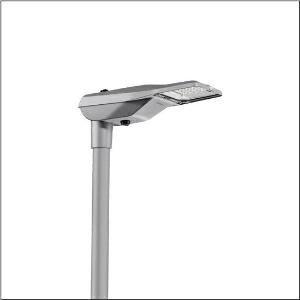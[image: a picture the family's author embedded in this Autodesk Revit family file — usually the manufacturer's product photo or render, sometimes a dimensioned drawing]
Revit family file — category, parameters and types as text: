
# Revit family: streetlight_sl_21_iq_micro___pl52_5xe1h31y08db_0e41
name_source: partatom
category: Lighting Fixtures
units: mm (PartAtom-declared; Revit-internal decimal feet)

## family parameters
Cut with Voids When Loaded = No
Host = Face
Light Source = No
Part Type = Normal
Room Calculation Point = No
Round Connector Dimension = Use Diameter
Shared = No

## types (1)
- --- (1 x LED, 5030 lm, 39.1 W, 3000K)
    Apparent Load = 39 VA
    CIE Flux Codes = 27 59 98 100 100
    Color Rendering = 70
    Color Temperature = 3000K
    Default Elevation = 1800 mm
    Description = Streetlight SL 21 iQ micro, mast luminaire, primary light control with lens, of PMMA, primary optical cover: cover, of toughened safety glass, transparent, light distribution: PL52, light emission: direct distribution, primary light characteristic: asymmetric, installation type: post-top, side-entry, LED, High Power LED, rated luminous flux: 5.030lm, luminous efficacy: 129lm/W, light colour: 730, colour temperature: 3000K, control: presetting dimming logarithmic, Street-Remote, Auto-Match, Temp-Guard, Lumen-Switch, Night-Set, Smart-Wire, Light-Fading, Desk-Remote (wireless, voltage-free reading and setting of iQ features in the workshop via application-optimized NFC function/RFID function), optimised constant luminous flux control (CLO 2.0), mains connection: 220..240V, AC, 50/60Hz, start of lifetime: 39W, end of service life: 41W, reduction: 17W, luminaire housing, of diecast aluminium, powder-coated, Siteco® metallic grey (DB 702S), corrosivity category C5 mid according to DIN EN ISO 12944, please order mast flange separately, inclination adjustable: 0°, 5°, 10°, 15°, sealing non-destructively replaceable, multi-level sealing system, length: 528mm, width: 235mm, height: 110mm, mast flange for spigot size: 42mm (side-entry): 5XC10008XM4, 60/48mm (side-entry/post-top): 5XC10108XM2, 76/60mm (side-entry/post-top): 5XC10108XM1, Smart Interface below and above, protection rating (complete): IP66, insulation class (complete): insulation class II (safety insulation), certification: CE, ENEC, ENEC+, VDE, impact resistance: IK09, permissible operating ambient temperature for outdoor applications: -40..+50°C, standard-compliant lighting for roads and squares, packaging unit: 1 piece

Light Distribution: PL52
    Height = 110 mm
    Lamp = 1 x LED
    Lamp Light Flux = 5030 lm
    Lamp Power = 39.1 W
    Lamp count = 1
    Length = 528 mm
    Luminous efficacy = 129 lm/W
    Manufacturer = Siteco
    ModVariant = No
    Model = 5XE1H31Y08DB
    Number of Poles = 1
    OnlyDefault = Yes
    Power Factor = 1
    Product Name = Streetlight SL 21 iQ micro | PL52
    Product group = mast luminaire | pylon top
    ProductGroupID = 6100
    Protection Class = Protection class II
    Protection Degree = IP 66
    RLX_Detail_Level = 1
    RLX_Emergency_Light_Flux = 0 lm
    RLX_Emergency_Type = 0
    RLX_Emergency_Type_DB = No
    RlxData = <blob elided: 108245 chars, md5=d88f797b>
    Socket = socket
    Standby Power = 0 W
    System Light Flux = 5030 lm
    System Power = 39 W
    Type Comments = factory setting: luminous flux: 100 % | dim-lin: 254 | 765 mA
    Type Image = l_1007239.jpg
    URL = http://relux.com
    VarID = @adj_046029
    Voltage = 0 V
    Weight = 0.00 kg
    Width = 235 mm

## geometry (parser evidence)
native form markers: Blend x4, Sweep x10
no freeform markers — native parametric forms only
